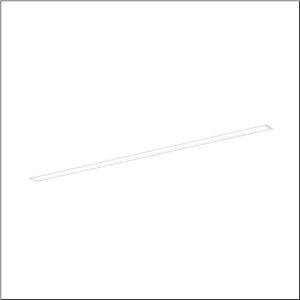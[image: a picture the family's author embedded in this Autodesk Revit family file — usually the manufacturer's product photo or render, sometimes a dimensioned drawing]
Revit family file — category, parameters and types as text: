
# Revit family: silica_r__21_51mx13db45wb_7b80
name_source: partatom
category: Lighting Fixtures
units: mm (PartAtom-declared; Revit-internal decimal feet)

## family parameters
Cut with Voids When Loaded = No
Host = Face
Light Source = No
Part Type = Normal
Room Calculation Point = No
Round Connector Dimension = Use Diameter
Shared = No

## types (1)
- --- (1 x LED, 4100 lm, 28.1 W, 4000K)
    Apparent Load = 28 VA
    CIE Flux Codes = 78 96 99 100 100
    Color Rendering = 80
    Color Temperature = 4000K
    Default Elevation = 1800 mm
    Description = Silica® 21, office luminaire, primary optical cover: prismatic diffuser, of PMMA, CAT 2 (L<= 3000cd/m²), light emission: direct distribution, primary light characteristic: symmetric, installation type: recessed, LED, rated luminous flux: 4.100lm, luminous efficacy: 146lm/W, light colour: 840, colour temperature: 4000K, with terminal, 3+2-pole, max. 2.5mm², mains connection: 220..240V, AC, 50/60Hz, rated input power: 28.1W, luminaire housing, of aluminium, traffic white (RAL 9016), length: 1.528mm, width: 79mm, height: 53mm, protection rating (complete): IP20, insulation class (complete): insulation class I (protective earthing), certification: CE, permissible operating ambient temperature: 0..+35°C, standard: EN 50419, packaging unit: 1 piece
    Height = 0 mm  [stored 0 ft]
    Lamp = 1 x LED
    Lamp Light Flux = 4100 lm
    Lamp Power = 28.1 W
    Lamp count = 1
    Length = 1527 mm
    Luminous efficacy = 146 lm/W
    Manufacturer = Siteco
    ModVariant = No
    Model = 51MX13DB45WB
    Mounting Place = Ceiling
    Mounting Type = Recessed
    Number of Poles = 1
    OnlyDefault = Yes
    Power Factor = 1
    Product Name = Silica® 21
    Product group = office luminaire | ceiling recessed
    ProductGroupID = 401
    Protection Class = Protection class I
    Protection Degree = IP 20
    RLX_Detail_Level = 1
    RLX_Emergency_Light_Flux = 0 lm
    RLX_Emergency_Type = 0
    RLX_Emergency_Type_DB = No
    RlxData = <blob elided: 14277 chars, md5=763ff60c>
    Socket = socket
    Standby Power = 0 W
    System Light Flux = 4100 lm
    System Power = 28 W
    Type Comments = factory setting: luminous flux: 100 % | dim-lin: 254 | 323 mA
    Type Image = l_1251692.jpg
    URL = http://relux.com
    VarID = @adj_067603
    Voltage = 0 V
    Weight = 0.00 kg
    Width = 79 mm

note: [stored X ft] marks values corroborated as IEEE doubles in the binary element streams (Revit-internal decimal feet)

## geometry (parser evidence)
native form markers: Sweep x12
no freeform markers — native parametric forms only
